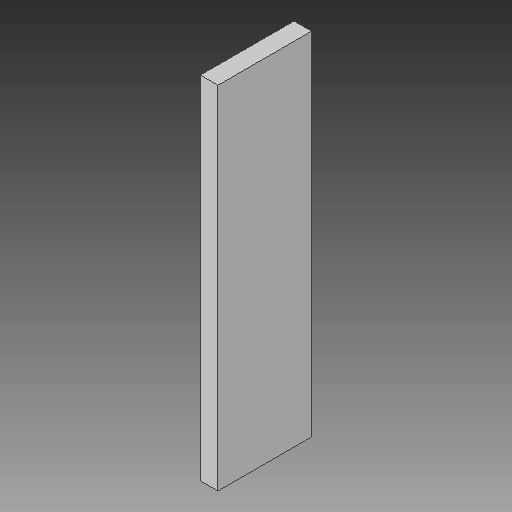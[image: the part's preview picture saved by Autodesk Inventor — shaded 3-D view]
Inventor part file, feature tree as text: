
AUTODESK INVENTOR PART (.ipt)
format: ipt  version: 2017 (Build 210142000, 142)  size: 89,088 bytes
history: native  units: in
note: dims shown in document units (in); Inventor stores cm internally (conversion verified against a paired STEP export)
features: sketch x2, extrude x1
ambient origin geometry x8: Origin, YZ Plane, XZ Plane, XY Plane, X Axis, Y Axis, Z Axis, Center Point
bodies: Solid1 (feature_tree)
feature tree (3):
  extrude  "Extrusion1"  Depth=3.0in
  sketch  "Sketch2"  dims[d2=0.8in d3=0.0in]
  sketch  "Sketch1"  dims[d0=0.15in d1=3.0in]
